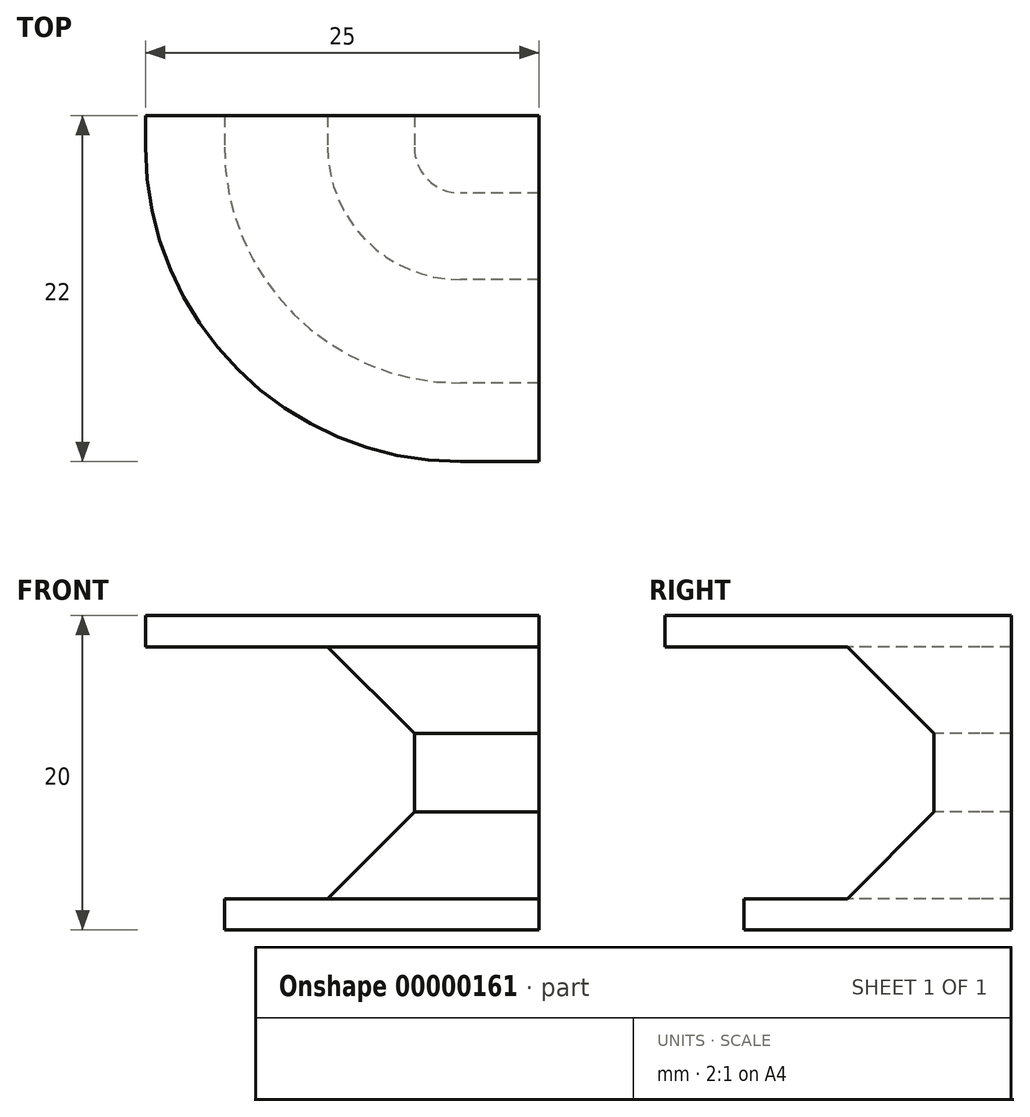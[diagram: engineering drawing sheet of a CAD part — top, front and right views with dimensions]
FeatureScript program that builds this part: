
annotation { "Feature Type Name" : "Feature", "Feature Type Description" : "" }
export const myFeature = defineFeature(function(context is Context, id is Id, definition is map)
    precondition{}
    {
        {
            var Q0;
            Q0 = qCreatedBy(makeId("Right.planeOp"), FACE);
            var sketch = newSketch(context, id + "F0", { "sketchPlane" : qUnion([Q0])});
            skLineSegment(sketch, "E0", {"start": v(0, 0) * mm, "end": v(0, 20) * mm});
            skLineSegment(sketch, "E1", {"start": v(0, 20) * mm, "end": v(-20, 20) * mm});
            skLineSegment(sketch, "E2", {"start": v(-20, 20) * mm, "end": v(-20, 18) * mm});
            skLineSegment(sketch, "E3", {"start": v(-20, 18) * mm, "end": v(-8.44, 18) * mm});
            skLineSegment(sketch, "E4", {"start": v(-8.44, 18) * mm, "end": v(-2.94, 12.5) * mm});
            skLineSegment(sketch, "E5", {"start": v(-2.94, 12.5) * mm, "end": v(-2.94, 7.5) * mm});
            skLineSegment(sketch, "E6", {"start": v(-2.94, 7.5) * mm, "end": v(-8.44, 2) * mm});
            skLineSegment(sketch, "E7", {"start": v(-8.44, 2) * mm, "end": v(-15, 2) * mm});
            skLineSegment(sketch, "E8", {"start": v(-15, 2) * mm, "end": v(-15, 0) * mm});
            skLineSegment(sketch, "E9", {"start": v(-15, 0) * mm, "end": v(0, 0) * mm});
            skLineSegment(sketch, "E10", {"start": v(-2.94, 12.5) * mm, "end": v(0, 12.5) * mm, "construction": true});
            skLineSegment(sketch, "E11", {"start": v(-2.94, 7.5) * mm, "end": v(0, 7.5) * mm, "construction": true});
            skSolve(sketch);
        }
        {
            var Q0;
            Q0=makeQuery(id+"F0.imprint","IMPRINT",FACE,{"disambiguationData":[TD([[makeQuery(id+"F0.imprint","IMPRINT",EDGE,{"derivedFrom":sQuery(id+"F0.wireOp",EDGE,"E0")}),1.0]])]});
            extrude(context, id + "F1", {"entities" : qUnion([Q0]), "depth" : 5 * mm});
        }
        {
            var Q0;
            Q0=makeQuery(id+"F0.imprint","IMPRINT",FACE,{"disambiguationData":[TD([[makeQuery(id+"F0.imprint","IMPRINT",EDGE,{"derivedFrom":sQuery(id+"F0.wireOp",EDGE,"E0")}),1.0]])]});
            var Q1;
            Q1=makeQuery(id+"F1.opExtrude","CAP_EDGE",EDGE,{"disambiguationData":[OSD([sQuery(id+"F0.wireOp",EDGE,"E0")])],"isStart":true});
            revolve(context, id + "F2", {"operationType" : NewBodyOperationType.ADD, "entities" : qUnion([Q0]), "axis" : qUnion([Q1]), "revolveType" : RevolveType.ONE_DIRECTION, "oppositeDirection" : true, "angle" : 90 * degree});
        }
        {
            var Q0;
            {var subQ0=sQuery(id+"F0.wireOp",EDGE,"E0");Q0=makeQuery(id+"F2.boolean.opBoolean","MERGE",FACE,{"derivedFrom":[makeQuery(id+"F1.opExtrude","SWEPT_FACE",FACE,{"disambiguationData":[OSD([subQ0])]}),makeQuery(id+"F2.opRevolve","CAP_FACE",FACE,{"disambiguationData":[OSD([subQ0,sQuery(id+"F0.wireOp",EDGE,"E1"),sQuery(id+"F0.wireOp",EDGE,"E2"),sQuery(id+"F0.wireOp",EDGE,"E3"),sQuery(id+"F0.wireOp",EDGE,"E4"),sQuery(id+"F0.wireOp",EDGE,"E5"),sQuery(id+"F0.wireOp",EDGE,"E6"),sQuery(id+"F0.wireOp",EDGE,"E7"),sQuery(id+"F0.wireOp",EDGE,"E8"),sQuery(id+"F0.wireOp",EDGE,"E9")])],"isStart":false})]});}
            extrude(context, id + "F3", {"entities" : qUnion([Q0]), "operationType" : NewBodyOperationType.ADD, "depth" : 2 * mm});
        }
    });
